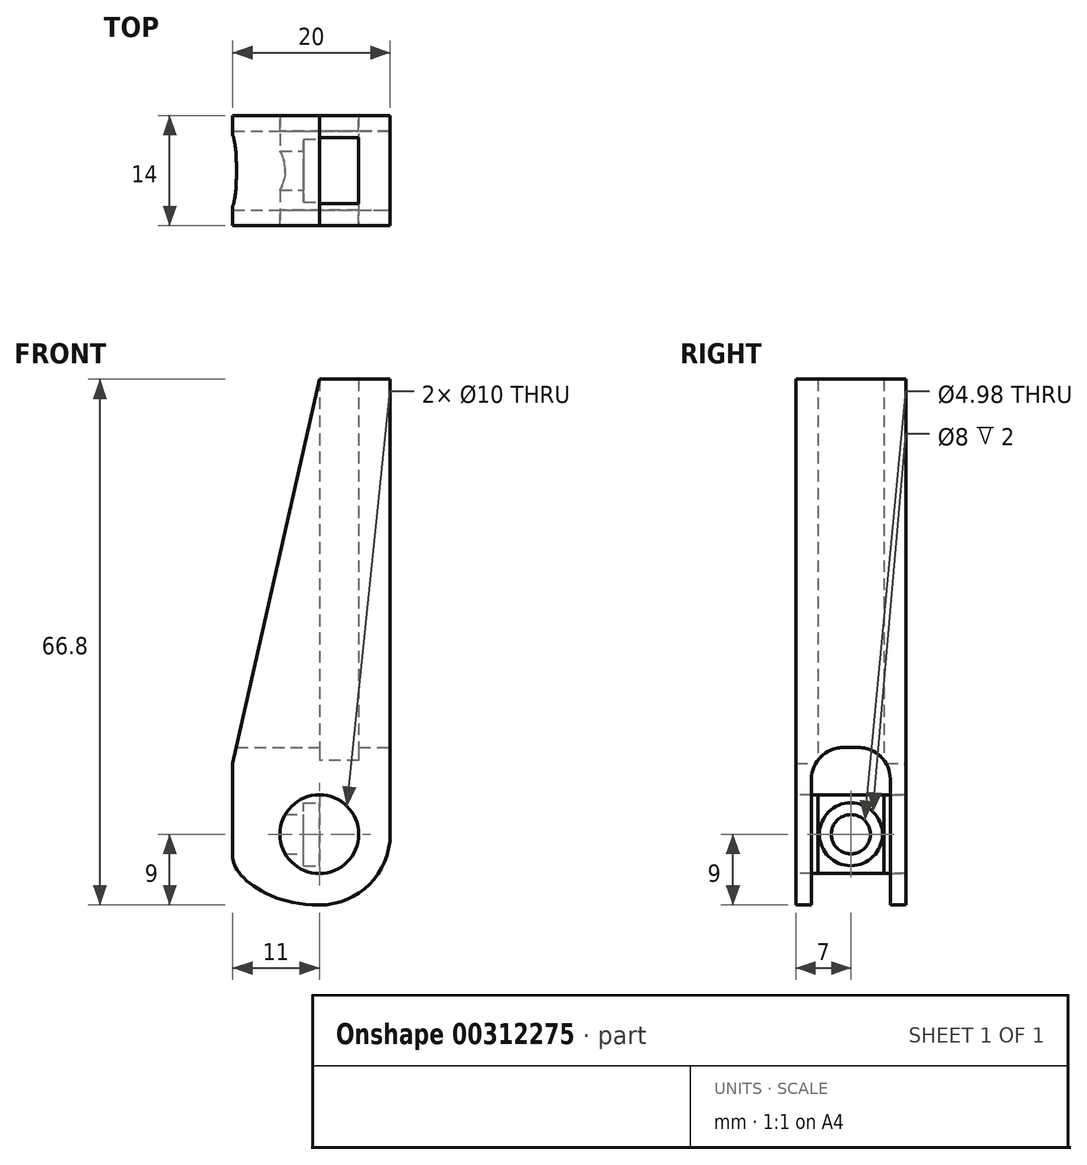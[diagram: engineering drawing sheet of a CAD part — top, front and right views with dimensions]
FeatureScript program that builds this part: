
annotation { "Feature Type Name" : "Feature", "Feature Type Description" : "" }
export const myFeature = defineFeature(function(context is Context, id is Id, definition is map)
    precondition{}
    {
        {
            var Q0;
            Q0=qCreatedBy(makeId("Front.planeOp"),FACE);
            var sketch = newSketch(context, id + "F0", { "sketchPlane" : qUnion([Q0])});
            skCircle(sketch, "E0", {"center": v(0, 9) * mm, "radius": 5 * mm});
            skLineSegment(sketch, "E1", {"start": v(9, 9) * mm, "end": v(9, 66.8) * mm});
            skLineSegment(sketch, "E2", {"start": v(9, 66.8) * mm, "end": v(0, 66.8) * mm});
            skLineSegment(sketch, "E3", {"start": v(0, 66.8) * mm, "end": v(-11, 18) * mm});
            skLineSegment(sketch, "E4", {"start": v(-11, 18) * mm, "end": v(-11, 6) * mm});
            skFitSpline(sketch, "E5", {"points": [v(-11, 6) * mm, v(0, 0) * mm], "startDerivative": vector(0, -6) * mm, "endDerivative": vector(21, 0) * mm});
            skLineSegment(sketch, "E6", {"start": v(0, 18) * mm, "end": v(-11, 18) * mm, "construction": true});
            skArc(sketch, "E7", {"start": v(9, 9) * mm, "mid": v(-6.36, 15.36) * mm, "end": v(0, 0) * mm, "construction": true});
            skArc(sketch, "E8", {"start": v(0, 0) * mm, "mid": v(6.36, 2.64) * mm, "end": v(9, 9) * mm});
            skSolve(sketch);
        }
        {
            var Q0;
            Q0=makeQuery(id+"F0.imprint","IMPRINT",FACE,{"disambiguationData":[TD([[makeQuery(id+"F0.imprint","IMPRINT",EDGE,{"derivedFrom":sQuery(id+"F0.wireOp",EDGE,"E0")}),-1.0]])]});
            extrude(context, id + "F1", {"entities" : qUnion([Q0]), "depth" : 14 * mm});
        }
        {
            var Q0;
            Q0=makeQuery(id+"F1.opExtrude","SWEPT_FACE",FACE,{"disambiguationData":[OSD([sQuery(id+"F0.wireOp",EDGE,"E1")])]});
            var sketch = newSketch(context, id + "F2", { "sketchPlane" : qUnion([Q0])});
            skLineSegment(sketch, "E9.0", {"start": v(-14, 4) * mm, "end": v(-14, 14) * mm, "construction": true});
            skLineSegment(sketch, "E10", {"start": v(-12, 20) * mm, "end": v(-12, 0) * mm});
            skLineSegment(sketch, "E11", {"start": v(-2, 0) * mm, "end": v(-2, 20) * mm});
            skLineSegment(sketch, "E12", {"start": v(-2, 20) * mm, "end": v(-12, 20) * mm});
            skLineSegment(sketch, "E13", {"start": v(-12, 0) * mm, "end": v(-2, 0) * mm});
            skSolve(sketch);
        }
        {
            var Q0;
            {var subQ0=sQuery(id+"F2.wireOp",EDGE,"E13");Q0=makeQuery(id+"F2.imprint","IMPRINT",FACE,{"disambiguationData":[TD([[makeQuery(id+"F2.imprint","IMPRINT",EDGE,{"derivedFrom":subQ0}),1.0]])]});}
            var Q1;
            {var subQ0=sQuery(id+"F2.wireOp",EDGE,"E12");Q1=makeQuery(id+"F2.imprint","IMPRINT",FACE,{"disambiguationData":[TD([[makeQuery(id+"F2.imprint","IMPRINT",EDGE,{"derivedFrom":subQ0}),1.0]])]});}
            extrude(context, id + "F3", {"entities" : qUnion([Q0, Q1]), "operationType" : NewBodyOperationType.REMOVE, "oppositeDirection" : true, "depth" : 25 * mm});
        }
        {
            var Q0;
            Q0=makeQuery(id+"F1.opExtrude","SWEPT_FACE",FACE,{"disambiguationData":[OSD([sQuery(id+"F0.wireOp",EDGE,"E2")])]});
            var sketch = newSketch(context, id + "F4", { "sketchPlane" : qUnion([Q0])});
            skLineSegment(sketch, "E14.0", {"start": v(-10.55, -2) * mm, "end": v(-10.55, -12) * mm});
            skLineSegment(sketch, "E15", {"start": v(-10.55, -2) * mm, "end": v(7, -2) * mm});
            skLineSegment(sketch, "E16", {"start": v(7, -12) * mm, "end": v(-10.55, -12) * mm});
            skLineSegment(sketch, "E17", {"start": v(7, -2) * mm, "end": v(7, -12) * mm});
            skSolve(sketch);
        }
        {
            var Q0;
            Q0=makeQuery(id+"F1.opExtrude","CAP_FACE",FACE,{"disambiguationData":[OSD([sQuery(id+"F0.wireOp",EDGE,"E0"),sQuery(id+"F0.wireOp",EDGE,"E1"),sQuery(id+"F0.wireOp",EDGE,"E2"),sQuery(id+"F0.wireOp",EDGE,"E3"),sQuery(id+"F0.wireOp",EDGE,"E4"),sQuery(id+"F0.wireOp",EDGE,"E5"),sQuery(id+"F0.wireOp",EDGE,"E8")])],"isStart":false});
            var sketch = newSketch(context, id + "F5", { "sketchPlane" : qUnion([Q0])});
            skCircle(sketch, "E18.0", {"center": v(0, 9) * mm, "radius": 5 * mm});
            skSolve(sketch);
        }
        {
            var Q0;
            Q0=makeQuery(id+"F5.imprint","IMPRINT",FACE,{"disambiguationData":[TD([[makeQuery(id+"F5.imprint","IMPRINT",EDGE,{"derivedFrom":sQuery(id+"F5.wireOp",EDGE,"E18.0")}),1.0]])]});
            var Q1;
            Q1=makeQuery(id+"F1.opExtrude","CAP_FACE",FACE,{"disambiguationData":[OSD([sQuery(id+"F0.wireOp",EDGE,"E0"),sQuery(id+"F0.wireOp",EDGE,"E1"),sQuery(id+"F0.wireOp",EDGE,"E2"),sQuery(id+"F0.wireOp",EDGE,"E3"),sQuery(id+"F0.wireOp",EDGE,"E4"),sQuery(id+"F0.wireOp",EDGE,"E5"),sQuery(id+"F0.wireOp",EDGE,"E8")])],"isStart":true});
            extrude(context, id + "F6", {"entities" : qUnion([Q0]), "endBound" : BoundingType.UP_TO_SURFACE, "oppositeDirection" : true, "endBoundEntityFace" : qUnion([Q1]), "depth" : 25 * mm});
        }
        {
            var Q0;
            Q0=qCreatedBy(makeId("Top.planeOp"),FACE);
            var sketch = newSketch(context, id + "F7", { "sketchPlane" : qUnion([Q0])});
            skLineSegment(sketch, "E19", {"start": v(5, -11.2) * mm, "end": v(5, -2.8) * mm});
            skLineSegment(sketch, "E20", {"start": v(5, -2.8) * mm, "end": v(0, -2.8) * mm});
            skLineSegment(sketch, "E21", {"start": v(0, -2.8) * mm, "end": v(0, -11.2) * mm});
            skLineSegment(sketch, "E22", {"start": v(0, -11.2) * mm, "end": v(5, -11.2) * mm});
            skSolve(sketch);
        }
        {
            var Q0;
            Q0=makeQuery(id+"F7.imprint","IMPRINT",FACE,{"disambiguationData":[TD([[makeQuery(id+"F7.imprint","IMPRINT",EDGE,{"derivedFrom":sQuery(id+"F7.wireOp",EDGE,"E19")}),1.0]])]});
            extrude(context, id + "F8", {"entities" : qUnion([Q0]), "operationType" : NewBodyOperationType.REMOVE, "endBound" : BoundingType.THROUGH_ALL, "depth" : 25 * mm});
        }
        {
            var Q0;
            Q0=makeQuery(id+"F8.boolean.opBoolean","COPY",FACE,{"derivedFrom":makeQuery(id+"F8.opExtrude","SWEPT_FACE",FACE,{"disambiguationData":[OSD([sQuery(id+"F7.wireOp",EDGE,"E21")])]})});
            var sketch = newSketch(context, id + "F9", { "sketchPlane" : qUnion([Q0])});
            skCircle(sketch, "E23", {"center": v(-7, 9) * mm, "radius": 4 * mm});
            skPoint(sketch, "E23.centerSnap0", {"position": v(-7, 4) * mm});
            skPoint(sketch, "E23.centerSnap1", {"position": v(-2.8, 9) * mm});
            skSolve(sketch);
        }
        {
            var Q0;
            Q0=sQuery(id+"F9.wireOp",VERTEX,"E23.center");
            var Q1;
            Q1=makeQuery(id+"F6.opExtrude","SWEPT_BODY",BODY,{"disambiguationData":[OSD([sQuery(id+"F5.wireOp",EDGE,"E18.0")])]});
            hole(context, id + "F10", {"style" : HoleStyle.SIMPLE, "endStyle" : HoleEndStyle.THROUGH, "standardTappedOrClearance" : lookupTablePath({ "standard" : "ANSI", "fit" : "Close", "size" : "#10", "type" : "Clearance" }), "standardBlindInLast" : lookupTablePath({ "fit" : "Close", "standard" : "ANSI", "size" : "#10", "type" : "Clearance" }), "holeDiameter" : 4.98 * mm, "isTappedThrough" : true, "tappedDepth" : 12 * mm, "tapClearance" : 3, "locations" : qUnion([Q0]), "scope" : qUnion([Q1])});
        }
        {
            var Q0;
            Q0=makeQuery(id+"F9.imprint","IMPRINT",FACE,{"disambiguationData":[TD([[makeQuery(id+"F9.imprint","IMPRINT",EDGE,{"derivedFrom":sQuery(id+"F9.wireOp",EDGE,"E23")}),1.0]])]});
            extrude(context, id + "F11", {"entities" : qUnion([Q0]), "operationType" : NewBodyOperationType.REMOVE, "oppositeDirection" : true, "depth" : 2 * mm});
        }
        {
            var Q0;
            Q0=makeQuery(id+"F3.boolean.opBoolean","COPY",EDGE,{"derivedFrom":makeQuery(id+"F3.opExtrude","SWEPT_EDGE",EDGE,{"disambiguationData":[OSD([sQuery(id+"F2.wireOp",EDGE,"E10"),sQuery(id+"F2.wireOp",EDGE,"E12")])]})});
            var Q1;
            Q1=makeQuery(id+"F3.boolean.opBoolean","COPY",EDGE,{"derivedFrom":makeQuery(id+"F3.opExtrude","SWEPT_EDGE",EDGE,{"disambiguationData":[OSD([sQuery(id+"F2.wireOp",EDGE,"E11"),sQuery(id+"F2.wireOp",EDGE,"E12")])]})});
            fillet(context, id + "F12", {"entities" : qUnion([Q0, Q1]), "radius" : 4 * mm, "tangentPropagation" : true, "allowEdgeOverflow" : false});
        }
    });
